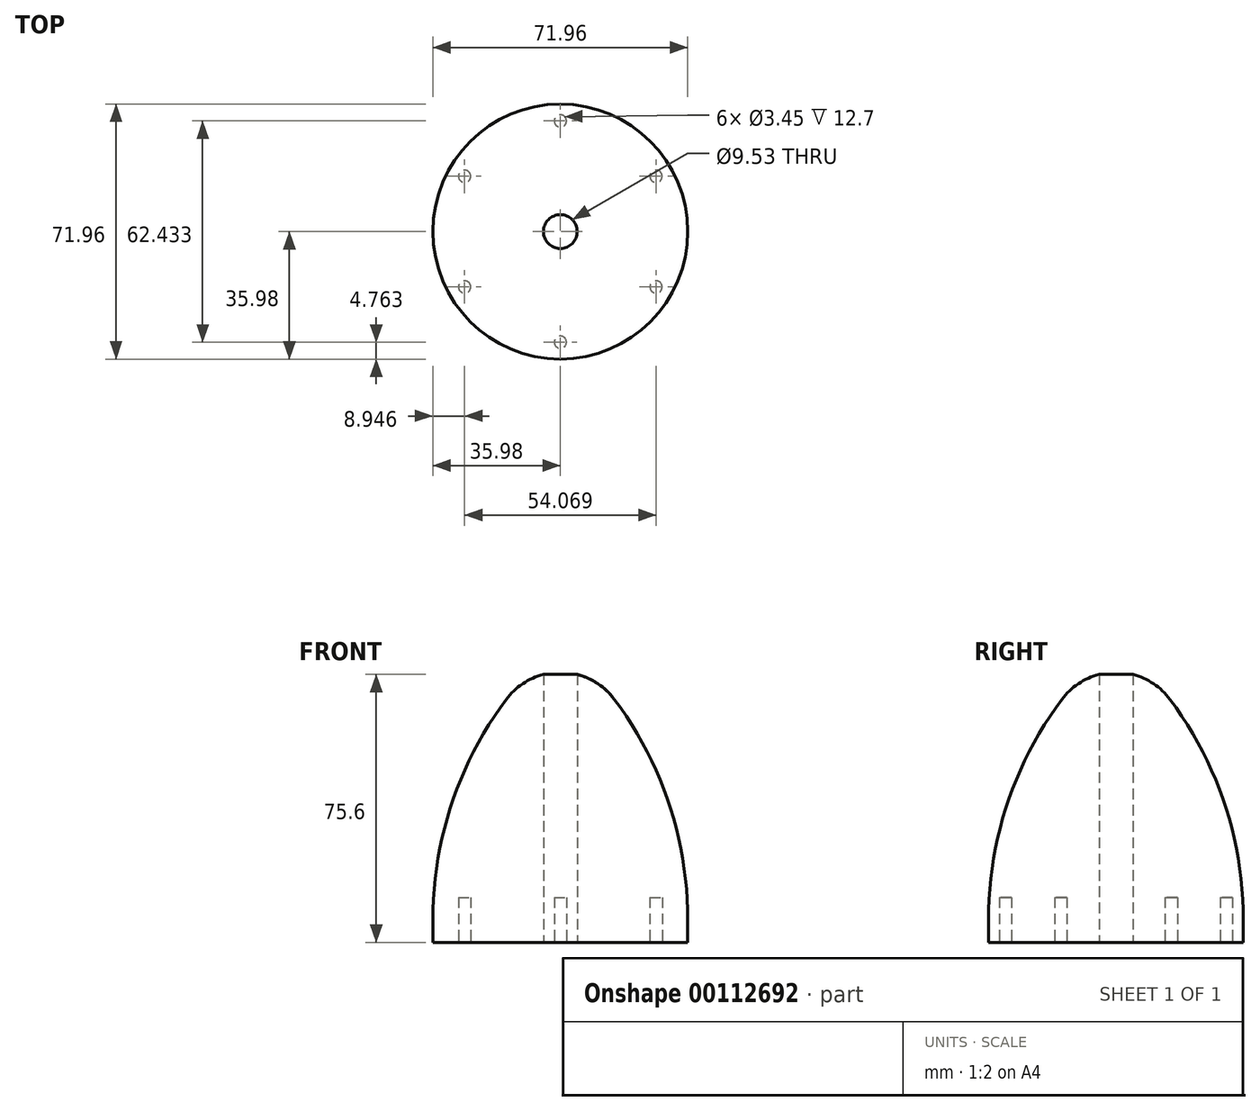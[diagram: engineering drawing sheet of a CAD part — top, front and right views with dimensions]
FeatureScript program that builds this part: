
annotation { "Feature Type Name" : "Feature", "Feature Type Description" : "" }
export const myFeature = defineFeature(function(context is Context, id is Id, definition is map)
    precondition{}
    {
        {
            var Q0;
            Q0=qCreatedBy(makeId("Top.planeOp"),FACE);
            var sketch = newSketch(context, id + "F0", { "sketchPlane" : qUnion([Q0])});
            skCircle(sketch, "E0", {"center": v(0, 0) * mm, "radius": 35.98 * mm});
            skSolve(sketch);
        }
        {
            var Q0;
            Q0 = qSketchRegion(id + "F0", true);
            extrude(context, id + "F1", {"entities" : qUnion([Q0]), "depth" : 76.2 * mm});
        }
        {
            var Q0;
            Q0=qCreatedBy(makeId("Front.planeOp"),FACE);
            var sketch = newSketch(context, id + "F2", { "sketchPlane" : qUnion([Q0])});
            skLineSegment(sketch, "E1", {"start": v(0, 0) * mm, "end": v(35.98, 0) * mm});
            skLineSegment(sketch, "E2", {"start": v(35.98, 0) * mm, "end": v(35.98, 6.35) * mm});
            skArc(sketch, "E3", {"start": v(15.24, 68.58) * mm, "mid": v(8.52, 74.19) * mm, "end": v(0, 76.2) * mm});
            skLineSegment(sketch, "E4", {"start": v(0, 0) * mm, "end": v(0, 76.2) * mm, "construction": true});
            skLineSegment(sketch, "E5", {"start": v(0, 76.2) * mm, "end": v(0, 112.18) * mm});
            skLineSegment(sketch, "E6", {"start": v(35.98, 6.35) * mm, "end": v(71.96, 6.35) * mm});
            skLineSegment(sketch, "E7", {"start": v(71.96, 6.35) * mm, "end": v(71.96, 112.18) * mm});
            skLineSegment(sketch, "E8", {"start": v(0, 112.18) * mm, "end": v(71.96, 112.18) * mm});
            skArc(sketch, "E9", {"start": v(35.98, 6.35) * mm, "mid": v(30.66, 39.15) * mm, "end": v(15.24, 68.58) * mm});
            skSolve(sketch);
        }
        {
            var Q0;
            Q0 = qSketchRegion(id + "F2", true);
            var Q1;
            Q1=makeQuery(id+"F1.opExtrude","CAP_EDGE",EDGE,{"disambiguationData":[OSD([sQuery(id+"F0.wireOp",EDGE,"E0")])],"isStart":false});
            revolve(context, id + "F3", {"operationType" : NewBodyOperationType.REMOVE, "entities" : qUnion([Q0]), "axis" : qUnion([Q1]), "revolveType" : RevolveType.FULL, "oppositeDirection" : true});
        }
        {
            var Q0;
            Q0=makeQuery(id+"F1.opExtrude","CAP_FACE",FACE,{"disambiguationData":[OSD([sQuery(id+"F0.wireOp",EDGE,"E0")])],"isStart":true});
            var sketch = newSketch(context, id + "F4", { "sketchPlane" : qUnion([Q0])});
            skCircle(sketch, "E10", {"center": v(0, 0) * mm, "radius": 4.76 * mm});
            skSolve(sketch);
        }
        {
            var Q0;
            Q0 = qSketchRegion(id + "F4", true);
            var Q1;
            Q1=makeQuery(id+"F3.boolean.opBoolean","COPY",FACE,{"derivedFrom":makeQuery(id+"F3.opRevolve","SWEPT_FACE",FACE,{"disambiguationData":[OSD([sQuery(id+"F2.wireOp",EDGE,"E9")])]})});
            extrude(context, id + "F5", {"entities" : qUnion([Q0]), "operationType" : NewBodyOperationType.REMOVE, "endBound" : BoundingType.UP_TO_SURFACE, "oppositeDirection" : true, "endBoundEntityFace" : qUnion([Q1]), "depth" : 25.4 * mm});
        }
        {
            var Q0;
            Q0=makeQuery(id+"F1.opExtrude","CAP_FACE",FACE,{"disambiguationData":[OSD([sQuery(id+"F0.wireOp",EDGE,"E0")])],"isStart":true});
            var sketch = newSketch(context, id + "F6", { "sketchPlane" : qUnion([Q0])});
            skCircle(sketch, "E11", {"center": v(-27.03, -15.6) * mm, "radius": 4.76 * mm, "construction": true});
            skCircle(sketch, "E12.cCircle", {"center": v(0, 0) * mm, "radius": 27.03 * mm, "construction": true});
            skLineSegment(sketch, "E12.0", {"start": v(27.03, 15.6) * mm, "end": v(27.03, -15.6) * mm, "construction": true});
            skLineSegment(sketch, "E12.1", {"start": v(27.03, -15.6) * mm, "end": v(0, -31.22) * mm, "construction": true});
            skLineSegment(sketch, "E12.2", {"start": v(0, -31.22) * mm, "end": v(-27.03, -15.6) * mm, "construction": true});
            skLineSegment(sketch, "E12.3", {"start": v(-27.03, -15.6) * mm, "end": v(-27.03, 15.6) * mm, "construction": true});
            skLineSegment(sketch, "E12.4", {"start": v(-27.03, 15.6) * mm, "end": v(0, 31.22) * mm, "construction": true});
            skLineSegment(sketch, "E12.5", {"start": v(0, 31.22) * mm, "end": v(27.03, 15.6) * mm, "construction": true});
            skPoint(sketch, "E12.0.midPoint", {"position": v(27.03, 0) * mm});
            skCircle(sketch, "E13", {"center": v(-27.03, -15.6) * mm, "radius": 1.73 * mm});
            skCircle(sketch, "E14", {"center": v(-27.03, 15.6) * mm, "radius": 1.73 * mm});
            skCircle(sketch, "E15", {"center": v(0, 31.22) * mm, "radius": 1.73 * mm});
            skCircle(sketch, "E16", {"center": v(27.03, 15.6) * mm, "radius": 1.73 * mm});
            skCircle(sketch, "E17", {"center": v(27.03, -15.6) * mm, "radius": 1.73 * mm});
            skCircle(sketch, "E18", {"center": v(0, -31.22) * mm, "radius": 1.73 * mm});
            skSolve(sketch);
        }
        {
            var Q0;
            Q0 = qSketchRegion(id + "F6", true);
            extrude(context, id + "F7", {"entities" : qUnion([Q0]), "operationType" : NewBodyOperationType.REMOVE, "oppositeDirection" : true, "depth" : 12.7 * mm});
        }
    });
